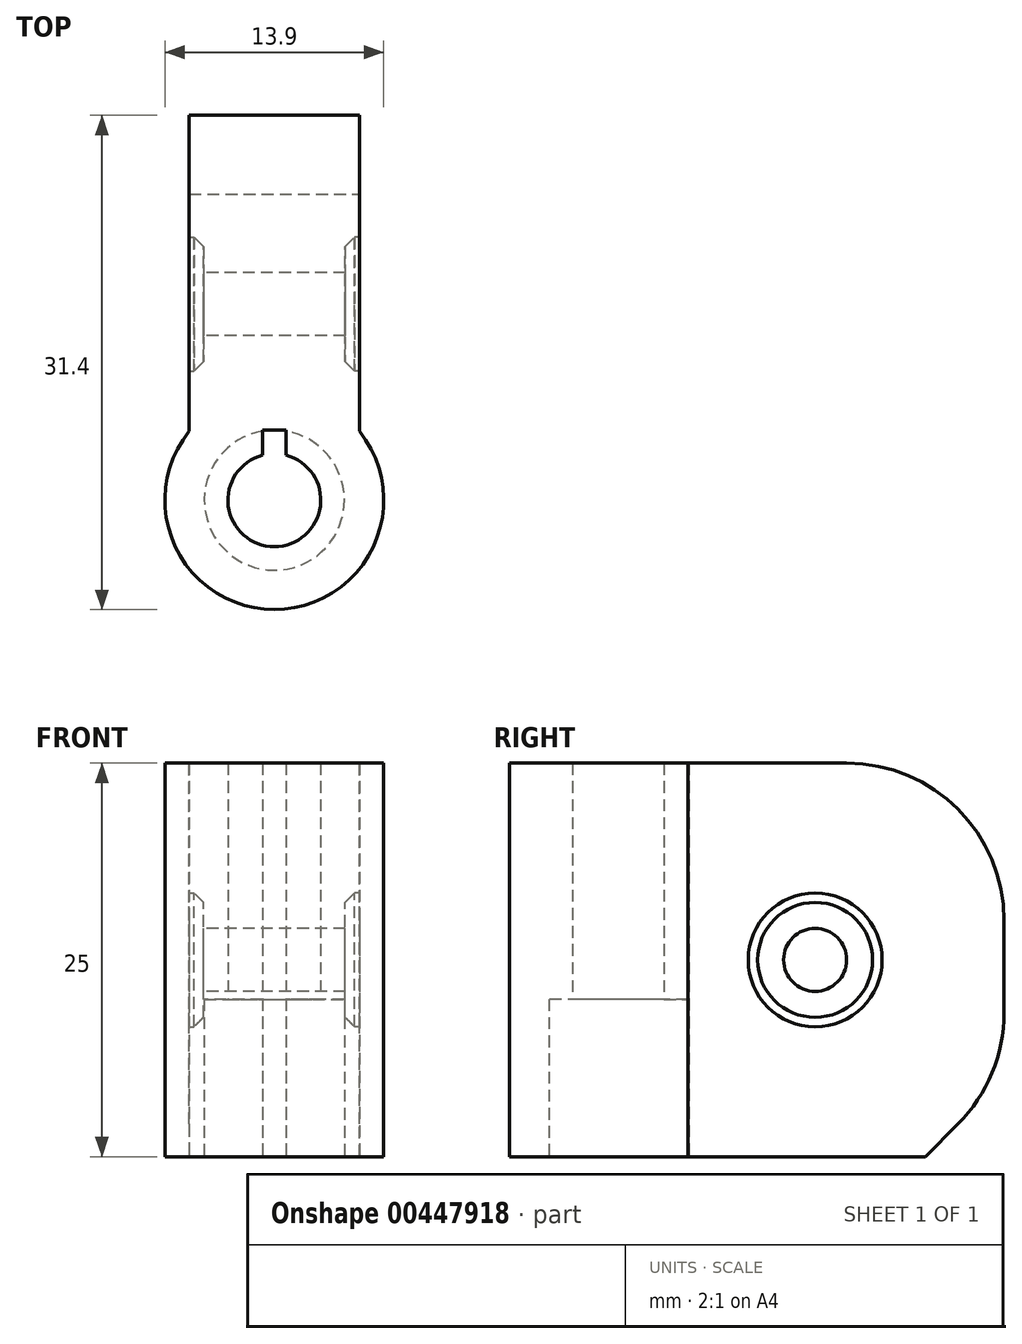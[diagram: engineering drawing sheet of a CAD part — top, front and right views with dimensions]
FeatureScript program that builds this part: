
annotation { "Feature Type Name" : "Feature", "Feature Type Description" : "" }
export const myFeature = defineFeature(function(context is Context, id is Id, definition is map)
    precondition{}
    {
        {
            var Q0;
            Q0=qCreatedBy(makeId("Top.planeOp"),FACE);
            var sketch = newSketch(context, id + "F0", { "sketchPlane" : qUnion([Q0])});
            skLineSegment(sketch, "E0", {"start": v(-5.4, 12) * mm, "end": v(5.4, 12) * mm});
            skPoint(sketch, "E1", {"position": v(0, 12) * mm});
            skLineSegment(sketch, "E2", {"start": v(-5.4, 12) * mm, "end": v(-5.4, -8.07) * mm});
            skArc(sketch, "E3", {"start": v(-0.75, -9.6) * mm, "mid": v(0, -15.4) * mm, "end": v(0.75, -9.6) * mm});
            skLineSegment(sketch, "E4.top", {"start": v(-0.75, -8) * mm, "end": v(0.75, -8) * mm});
            skLineSegment(sketch, "E4.left", {"start": v(-0.75, -9.6) * mm, "end": v(-0.75, -8) * mm});
            skLineSegment(sketch, "E4.right", {"start": v(0.75, -9.6) * mm, "end": v(0.75, -8) * mm});
            skPoint(sketch, "E4.middle", {"position": v(0, -9.5) * mm});
            skPoint(sketch, "E4.bottom.start.orphan", {"position": v(-0.75, -11) * mm});
            skPoint(sketch, "E5.orphan", {"position": v(0.75, -11) * mm});
            skLineSegment(sketch, "E6.bottom", {"start": v(-5.4, -2) * mm, "end": v(5.4, -2) * mm, "construction": true});
            skLineSegment(sketch, "E6.top", {"start": v(-5.4, 2) * mm, "end": v(5.4, 2) * mm, "construction": true});
            skLineSegment(sketch, "E6.left", {"start": v(-5.4, -2) * mm, "end": v(-5.4, 2) * mm});
            skLineSegment(sketch, "E6.right", {"start": v(5.4, -2) * mm, "end": v(5.4, 2) * mm});
            skPoint(sketch, "E6.middle", {"position": v(0, 0) * mm});
            skArc(sketch, "E7", {"start": v(-5.4, -8.07) * mm, "mid": v(0, -19.4) * mm, "end": v(5.4, -8.07) * mm});
            skLineSegment(sketch, "E8", {"start": v(5.4, 12) * mm, "end": v(5.4, -8.07) * mm});
            skCircle(sketch, "E9", {"center": v(0, -12.45) * mm, "radius": 4.45 * mm});
            skSolve(sketch);
        }
        {
            var Q0;
            {var subQ3=sQuery(id+"F0.wireOp",EDGE,"E0");Q0=makeQuery(id+"F0.imprint","IMPRINT",FACE,{"disambiguationData":[TD([[makeQuery(id+"F0.imprint","IMPRINT",EDGE,{"derivedFrom":subQ3}),-1.0]])]});}
            var Q1;
            {var subQ0=sQuery(id+"F0.wireOp",EDGE,"E3");Q1=makeQuery(id+"F0.imprint","IMPRINT",FACE,{"disambiguationData":[TD([[makeQuery(id+"F0.imprint","IMPRINT",EDGE,{"derivedFrom":subQ0}),-1.0]])]});}
            extrude(context, id + "F1", {"entities" : qUnion([Q0, Q1]), "depth" : 25 * mm});
        }
        {
            var Q0;
            Q0=makeQuery(id+"F1.opExtrude","CAP_EDGE",EDGE,{"disambiguationData":[OSD([sQuery(id+"F0.wireOp",EDGE,"E0")])],"isStart":false});
            fillet(context, id + "F2", {"entities" : qUnion([Q0]), "radius" : 10 * mm, "tangentPropagation" : true, "allowEdgeOverflow" : false});
        }
        {
            var Q0;
            Q0=qCreatedBy(makeId("Right.planeOp"),FACE);
            var sketch = newSketch(context, id + "F3", { "sketchPlane" : qUnion([Q0])});
            skPoint(sketch, "E10.0", {"position": v(-8.07, 12.5) * mm});
            skLineSegment(sketch, "E11", {"start": v(-8.07, 12.5) * mm, "end": v(0, 12.5) * mm, "construction": true});
            skCircle(sketch, "E12", {"center": v(0, 12.5) * mm, "radius": 2 * mm});
            skCircle(sketch, "E13", {"center": v(0, 12.5) * mm, "radius": 4.25 * mm});
            skSolve(sketch);
        }
        {
            var Q0;
            Q0=makeQuery(id+"F3.imprint","IMPRINT",FACE,{"disambiguationData":[TD([[makeQuery(id+"F3.imprint","IMPRINT",EDGE,{"derivedFrom":sQuery(id+"F3.wireOp",EDGE,"E12")}),1.0]])]});
            extrude(context, id + "F4", {"entities" : qUnion([Q0]), "operationType" : NewBodyOperationType.REMOVE, "endBound" : BoundingType.SYMMETRIC, "depth" : 25 * mm});
        }
        {
            var Q0;
            Q0=makeQuery(id+"F1.opExtrude","CAP_EDGE",EDGE,{"disambiguationData":[OSD([sQuery(id+"F0.wireOp",EDGE,"E0")])],"isStart":true});
            chamfer(context, id + "F5", {"entities" : qUnion([Q0]), "width" : 5 * mm, "tangentPropagation" : true});
        }
        {
            var Q0;
            {var subQ0=sQuery(id+"F0.wireOp",EDGE,"E3");Q0=makeQuery(id+"F0.imprint","IMPRINT",FACE,{"disambiguationData":[TD([[makeQuery(id+"F0.imprint","IMPRINT",EDGE,{"derivedFrom":subQ0}),-1.0]])]});}
            extrude(context, id + "F6", {"entities" : qUnion([Q0]), "operationType" : NewBodyOperationType.REMOVE, "depth" : 10 * mm});
        }
        {
            var Q0;
            Q0=makeQuery(id+"F3.imprint","IMPRINT",FACE,{"disambiguationData":[TD([[makeQuery(id+"F3.imprint","IMPRINT",EDGE,{"derivedFrom":sQuery(id+"F3.wireOp",EDGE,"E12")}),-1.0]])]});
            var Q1;
            Q1=makeQuery(id+"F1.opExtrude","SWEPT_FACE",FACE,{"disambiguationData":[OSD([sQuery(id+"F0.wireOp",EDGE,"E2"),sQuery(id+"F0.wireOp",EDGE,"E6.left")])]});
            extrude(context, id + "F7", {"entities" : qUnion([Q0]), "operationType" : NewBodyOperationType.REMOVE, "endBound" : BoundingType.UP_TO_SURFACE, "oppositeDirection" : true, "endBoundEntityFace" : qUnion([Q1]), "depth" : 25 * mm, "hasSecondDirection" : true, "secondDirectionOppositeDirection" : true, "secondDirectionDepth" : 4.5 * mm});
        }
        {
            var Q0;
            Q0=makeQuery(id+"F3.imprint","IMPRINT",FACE,{"disambiguationData":[TD([[makeQuery(id+"F3.imprint","IMPRINT",EDGE,{"derivedFrom":sQuery(id+"F3.wireOp",EDGE,"E12")}),-1.0]])]});
            var Q1;
            Q1=makeQuery(id+"F1.opExtrude","SWEPT_FACE",FACE,{"disambiguationData":[OSD([sQuery(id+"F0.wireOp",EDGE,"E8")])]});
            extrude(context, id + "F8", {"entities" : qUnion([Q0]), "operationType" : NewBodyOperationType.REMOVE, "endBound" : BoundingType.UP_TO_SURFACE, "endBoundEntityFace" : qUnion([Q1]), "depth" : 4.5 * mm, "hasSecondDirection" : true, "secondDirectionOppositeDirection" : false, "secondDirectionDepth" : 4.5 * mm});
        }
        {
            var Q0;
            Q0=makeQuery(id+"F8.boolean.opBoolean","COPY",EDGE,{"derivedFrom":makeQuery(id+"F8.opExtrude","CAP_EDGE",EDGE,{"disambiguationData":[OSD([sQuery(id+"F3.wireOp",EDGE,"E13")])],"isStart":true})});
            var Q1;
            Q1=makeQuery(id+"F7.boolean.opBoolean","COPY",EDGE,{"derivedFrom":makeQuery(id+"F7.opExtrude","CAP_EDGE",EDGE,{"disambiguationData":[OSD([sQuery(id+"F3.wireOp",EDGE,"E13")])],"isStart":true})});
            chamfer(context, id + "F9", {"entities" : qUnion([Q0, Q1]), "width" : .6 * mm, "tangentPropagation" : true});
        }
        {
            var Q0;
            {var subQ0=sQuery(id+"F0.wireOp",EDGE,"E0");Q0=makeQuery(id+"F5.opChamfer","BLEND_EDGE",EDGE,{"blendedFrom":[makeQuery(id+"F1.opExtrude","CAP_EDGE",EDGE,{"disambiguationData":[OSD([subQ0])],"isStart":true}),makeQuery(id+"F1.opExtrude","SWEPT_FACE",FACE,{"disambiguationData":[OSD([subQ0])]})],"blendedInto":[makeQuery(id+"F1.opExtrude","SWEPT_FACE",FACE,{"disambiguationData":[OSD([subQ0])]})]});}
            fillet(context, id + "F10", {"entities" : qUnion([Q0]), "radius" : 10 * mm, "tangentPropagation" : true, "allowEdgeOverflow" : false});
        }
    });
